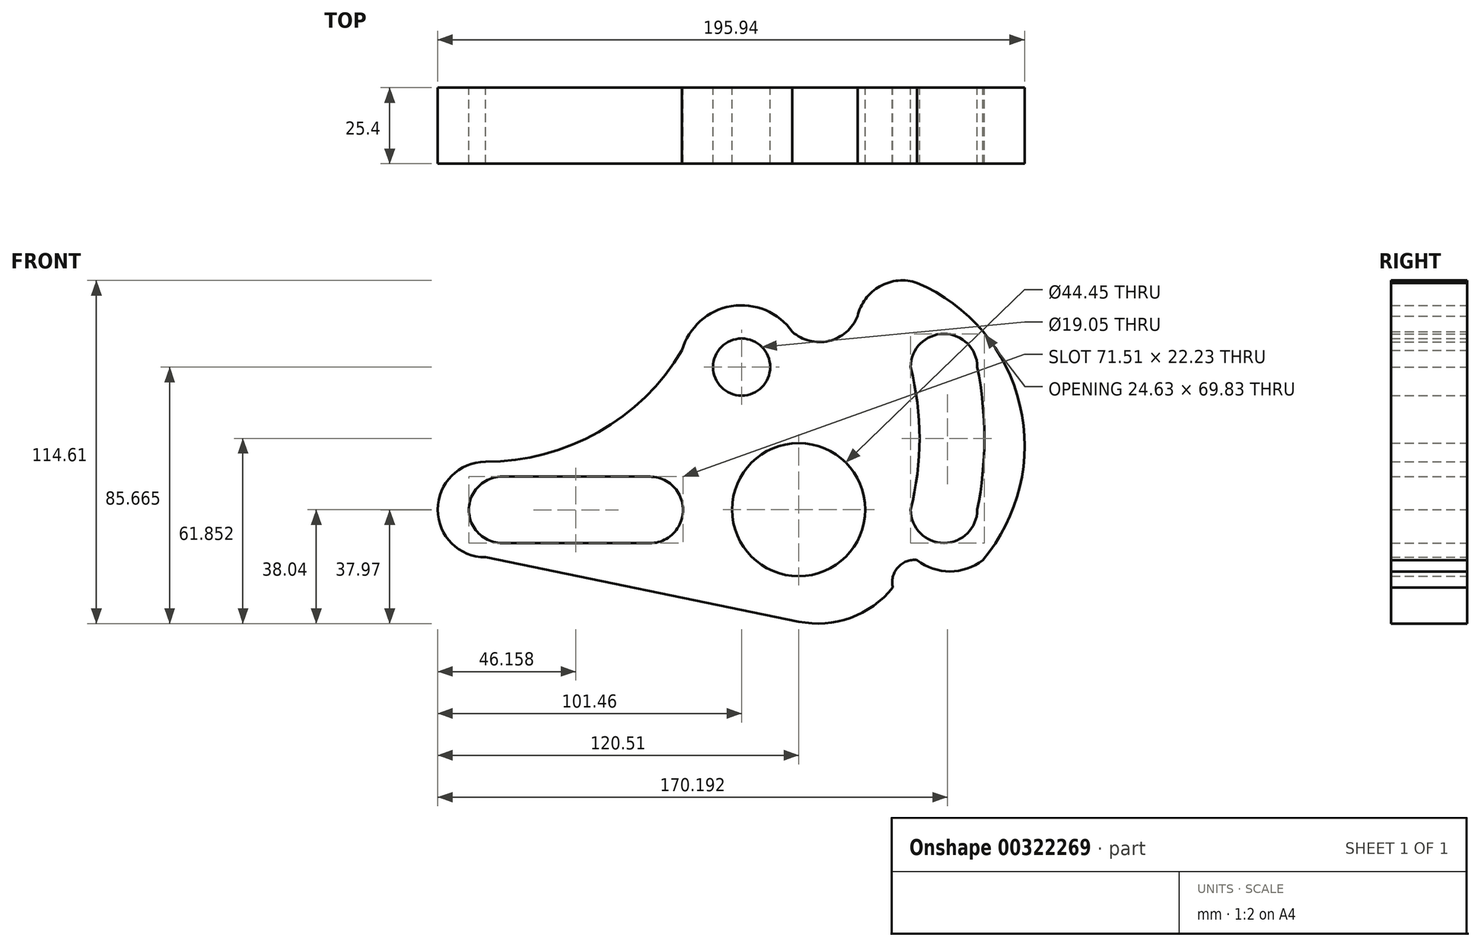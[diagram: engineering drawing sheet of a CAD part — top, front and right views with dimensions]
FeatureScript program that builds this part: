
annotation { "Feature Type Name" : "Feature", "Feature Type Description" : "" }
export const myFeature = defineFeature(function(context is Context, id is Id, definition is map)
    precondition{}
    {
        {
            var Q0;
            Q0=qCreatedBy(makeId("Front.planeOp"),FACE);
            var sketch = newSketch(context, id + "F0", { "sketchPlane" : qUnion([Q0])});
            skCircle(sketch, "E0", {"center": v(0, 0) * mm, "radius": 14.29 * mm});
            skCircle(sketch, "E1", {"center": v(0, 0) * mm, "radius": 22.23 * mm});
            skCircle(sketch, "E2", {"center": v(-19.05, 47.63) * mm, "radius": 20.64 * mm});
            skCircle(sketch, "E3", {"center": v(-19.05, 47.63) * mm, "radius": 9.53 * mm});
            skArc(sketch, "E4", {"start": v(37.37, 0) * mm, "mid": v(48.5, -11.1) * mm, "end": v(59.62, 0) * mm});
            skArc(sketch, "E5", {"start": v(59.62, 47.63) * mm, "mid": v(48.5, 58.73) * mm, "end": v(37.37, 47.63) * mm});
            skArc(sketch, "E6", {"start": v(-99, 11.05) * mm, "mid": v(-110.1, -0.05) * mm, "end": v(-99, -11.15) * mm});
            skLineSegment(sketch, "E7", {"start": v(-99, 11.05) * mm, "end": v(-49.7, 11.01) * mm});
            skLineSegment(sketch, "E8", {"start": v(-49.7, 11.01) * mm, "end": v(-99, 11.05) * mm});
            skLineSegment(sketch, "E9", {"start": v(-99, -11.15) * mm, "end": v(-49.7, -11.19) * mm});
            skArc(sketch, "E10", {"start": v(-49.7, -11.19) * mm, "mid": v(-38.6, -0.09) * mm, "end": v(-49.7, 11.01) * mm});
            skLineSegment(sketch, "E11", {"start": v(-104.55, 15.99) * mm, "end": v(-44.15, 15.99) * mm});
            skLineSegment(sketch, "E12", {"start": v(-104.55, -15.92) * mm, "end": v(-44.15, -15.92) * mm});
            skPoint(sketch, "E12.endSnap0", {"position": v(-44.15, -0.04) * mm});
            skArc(sketch, "E13", {"start": v(-104.55, 15.99) * mm, "mid": v(-120.5, 0.04) * mm, "end": v(-104.55, -15.92) * mm});
            skArc(sketch, "E14", {"start": v(-44.15, -15.92) * mm, "mid": v(-28.2, 0.04) * mm, "end": v(-44.15, 15.99) * mm});
            skArc(sketch, "E15", {"start": v(-104.55, 15.99) * mm, "mid": v(-66.82, 25.94) * mm, "end": v(-38.92, 53.21) * mm});
            skLineSegment(sketch, "E16", {"start": v(-104.55, -15.92) * mm, "end": v(0, -37.39) * mm});
            skArc(sketch, "E17", {"start": v(0, -37.39) * mm, "mid": v(17.31, -36.13) * mm, "end": v(31.43, -26.03) * mm});
            skArc(sketch, "E18", {"start": v(39.57, -16.81) * mm, "mid": v(33.1, -19.3) * mm, "end": v(31.43, -26.03) * mm});
            skArc(sketch, "E19", {"start": v(39.57, -16.81) * mm, "mid": v(50.5, -20.64) * mm, "end": v(61.42, -16.81) * mm});
            skArc(sketch, "E20", {"start": v(-4.65, 62.41) * mm, "mid": v(8.17, 56.04) * mm, "end": v(19.64, 64.6) * mm});
            skArc(sketch, "E21", {"start": v(39.57, 75.75) * mm, "mid": v(27.12, 74.62) * mm, "end": v(19.64, 64.6) * mm});
            skArc(sketch, "E22", {"start": v(37.37, 0) * mm, "mid": v(40.35, 23.81) * mm, "end": v(37.37, 47.63) * mm});
            skArc(sketch, "E23", {"start": v(59.62, 0) * mm, "mid": v(62, 23.81) * mm, "end": v(59.62, 47.63) * mm});
            skArc(sketch, "E24", {"start": v(61.42, -16.81) * mm, "mid": v(73.85, 34.98) * mm, "end": v(39.57, 75.75) * mm});
            skSolve(sketch);
        }
        {
            var Q0;
            Q0 = qSketchRegion(id + "F0", true);
            extrude(context, id + "F1", {"entities" : qUnion([Q0]), "depth" : 25.4 * mm});
        }
    });
